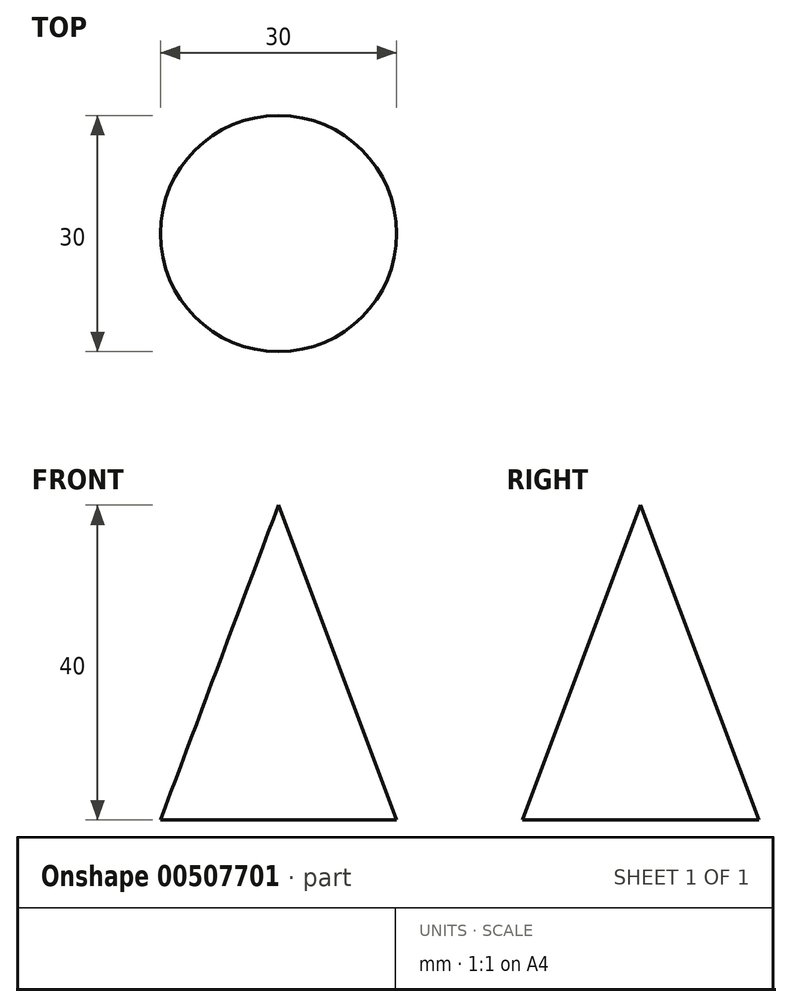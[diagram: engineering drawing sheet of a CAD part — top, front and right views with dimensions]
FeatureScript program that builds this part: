
annotation { "Feature Type Name" : "Feature", "Feature Type Description" : "" }
export const myFeature = defineFeature(function(context is Context, id is Id, definition is map)
    precondition{}
    {
        {
            var Q0;
            Q0=qCreatedBy(makeId("Front.planeOp"),FACE);
            var sketch = newSketch(context, id + "F0", { "sketchPlane" : qUnion([Q0])});
            skLineSegment(sketch, "E0", {"start": v(0, 40) * mm, "end": v(0, 0) * mm});
            skLineSegment(sketch, "E1", {"start": v(0, 0) * mm, "end": v(-15, 0) * mm});
            skLineSegment(sketch, "E2", {"start": v(-15, 0) * mm, "end": v(0, 40) * mm});
            skSolve(sketch);
        }
        {
            var Q0;
            Q0=makeQuery(id+"F0.imprint","IMPRINT",FACE,{"disambiguationData":[TD([[makeQuery(id+"F0.imprint","IMPRINT",EDGE,{"derivedFrom":sQuery(id+"F0.wireOp",EDGE,"E0")}),-1.0]])]});
            var Q1;
            Q1=sQuery(id+"F0.wireOp",EDGE,"E0");
            revolve(context, id + "F1", {"entities" : qUnion([Q0]), "axis" : qUnion([Q1]), "revolveType" : RevolveType.FULL});
        }
    });
